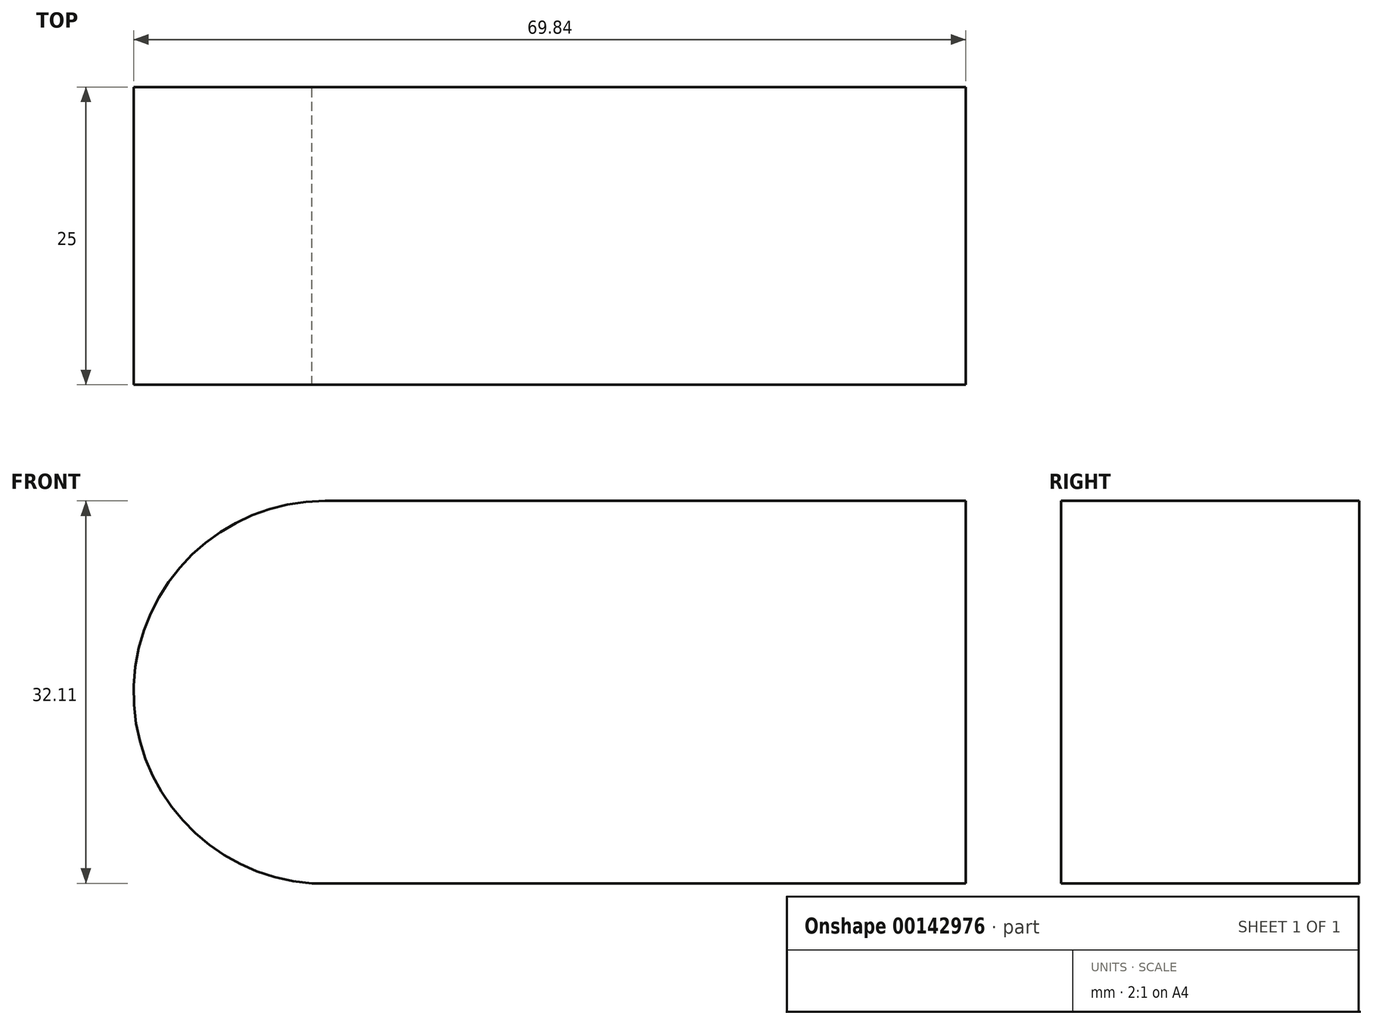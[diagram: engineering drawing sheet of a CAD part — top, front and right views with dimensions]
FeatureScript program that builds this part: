
annotation { "Feature Type Name" : "Feature", "Feature Type Description" : "" }
export const myFeature = defineFeature(function(context is Context, id is Id, definition is map)
    precondition{}
    {
        {
            var Q0;
            Q0=qCreatedBy(makeId("Front.planeOp"),FACE);
            var sketch = newSketch(context, id + "F0", { "sketchPlane" : qUnion([Q0])});
            skLineSegment(sketch, "E0", {"start": v(-46.62, 42.73) * mm, "end": v(5.38, 42.73) * mm});
            skArc(sketch, "E1", {"start": v(-46.62, 42.73) * mm, "mid": v(-62.68, 27.21) * mm, "end": v(-47.73, 10.62) * mm});
            skLineSegment(sketch, "E2", {"start": v(-47.73, 10.62) * mm, "end": v(4.27, 10.62) * mm});
            skLineSegment(sketch, "E3", {"start": v(4.27, 10.62) * mm, "end": v(7.15, 10.62) * mm});
            skLineSegment(sketch, "E4", {"start": v(7.15, 10.62) * mm, "end": v(7.15, 42.73) * mm});
            skLineSegment(sketch, "E5", {"start": v(7.15, 42.73) * mm, "end": v(5.38, 42.73) * mm});
            skSolve(sketch);
        }
        {
            var Q0;
            Q0=makeQuery(id+"F0.imprint","IMPRINT",FACE,{"disambiguationData":[TD([[makeQuery(id+"F0.imprint","IMPRINT",EDGE,{"derivedFrom":sQuery(id+"F0.wireOp",EDGE,"E0")}),-1.0]])]});
            extrude(context, id + "F1", {"entities" : qUnion([Q0]), "depth" : 25 * mm});
        }
    });
